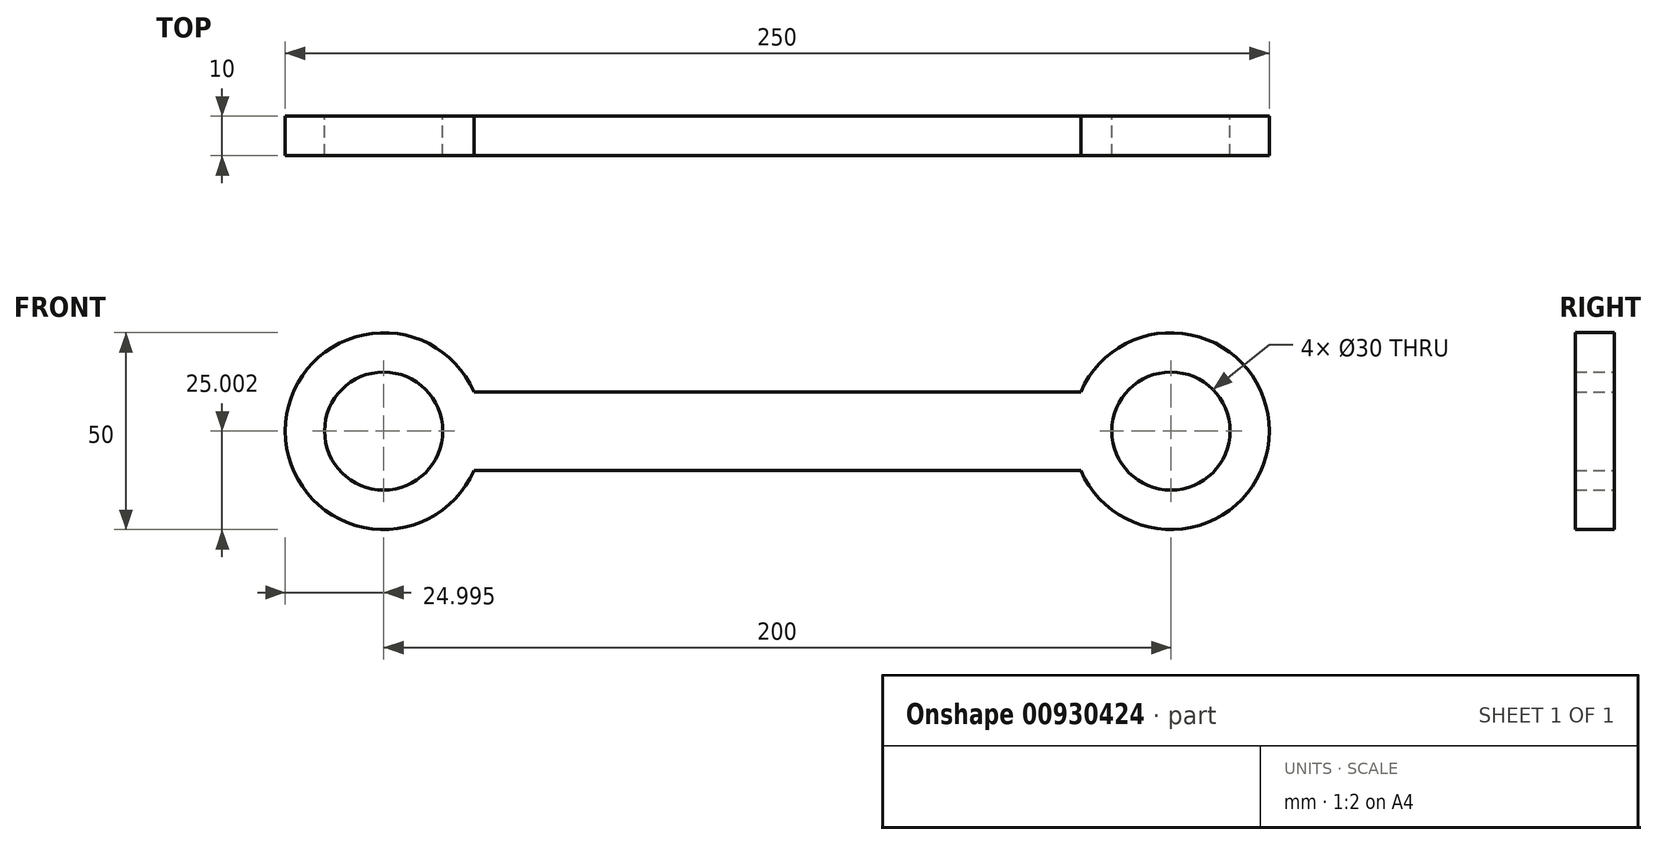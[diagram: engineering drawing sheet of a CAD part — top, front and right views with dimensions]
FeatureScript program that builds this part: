
annotation { "Feature Type Name" : "Feature", "Feature Type Description" : "" }
export const myFeature = defineFeature(function(context is Context, id is Id, definition is map)
    precondition{}
    {
        {
            var Q0;
            Q0=qCreatedBy(makeId("Front.planeOp"),FACE);
            var sketch = newSketch(context, id + "F0", { "sketchPlane" : qUnion([Q0])});
            skLineSegment(sketch, "E0.bottom", {"start": v(235.24, 10.47) * mm, "end": v(35.24, 10.47) * mm});
            skLineSegment(sketch, "E0.top", {"start": v(235.24, 30.47) * mm, "end": v(35.24, 30.47) * mm});
            skLineSegment(sketch, "E0.left", {"start": v(235.24, 10.47) * mm, "end": v(235.24, 30.47) * mm});
            skLineSegment(sketch, "E0.right", {"start": v(35.24, 10.47) * mm, "end": v(35.24, 30.47) * mm});
            skCircle(sketch, "E1", {"center": v(235.24, 20.47) * mm, "radius": 25 * mm});
            skCircle(sketch, "E2", {"center": v(235.24, 20.47) * mm, "radius": 15 * mm});
            skCircle(sketch, "E3", {"center": v(35.24, 20.47) * mm, "radius": 25 * mm});
            skCircle(sketch, "E4", {"center": v(35.24, 20.47) * mm, "radius": 15 * mm});
            skSolve(sketch);
        }
        {
            var Q0;
            {var subQ0=sQuery(id+"F0.wireOp",EDGE,"E1");var subQ1=sQuery(id+"F0.wireOp",EDGE,"E0.bottom");var subQ2=makeQuery(id+"F0.imprint","INTERSECT",VERTEX,{"derivedFrom":[subQ1,subQ0]});Q0=makeQuery(id+"F0.imprint","IMPRINT",FACE,{"disambiguationData":[TD([[makeQuery(id+"F0.imprint","IMPRINT",EDGE,{"disambiguationData":[TD([[subQ2,1.0]])],"derivedFrom":subQ1}),1.0]])]});}
            var Q1;
            {var subQ0=sQuery(id+"F0.wireOp",EDGE,"E1");var subQ1=sQuery(id+"F0.wireOp",EDGE,"E0.bottom");var subQ2=makeQuery(id+"F0.imprint","INTERSECT",VERTEX,{"derivedFrom":[subQ1,subQ0]});Q1=makeQuery(id+"F0.imprint","IMPRINT",FACE,{"disambiguationData":[TD([[makeQuery(id+"F0.imprint","IMPRINT",EDGE,{"disambiguationData":[TD([[subQ2,1.0]])],"derivedFrom":subQ1}),-1.0]])]});}
            var Q2;
            {var subQ0=sQuery(id+"F0.wireOp",EDGE,"E1");var subQ1=sQuery(id+"F0.wireOp",EDGE,"E0.bottom");var subQ2=makeQuery(id+"F0.imprint","INTERSECT",VERTEX,{"derivedFrom":[subQ1,subQ0]});Q2=makeQuery(id+"F0.imprint","IMPRINT",FACE,{"disambiguationData":[TD([[makeQuery(id+"F0.imprint","IMPRINT",EDGE,{"disambiguationData":[TD([[subQ2,-1.0]])],"derivedFrom":subQ1}),-1.0]])]});}
            var Q3;
            {var subQ0=sQuery(id+"F0.wireOp",EDGE,"E3");var subQ1=sQuery(id+"F0.wireOp",EDGE,"E0.bottom");var subQ2=makeQuery(id+"F0.imprint","INTERSECT",VERTEX,{"derivedFrom":[subQ1,subQ0]});Q3=makeQuery(id+"F0.imprint","IMPRINT",FACE,{"disambiguationData":[TD([[makeQuery(id+"F0.imprint","IMPRINT",EDGE,{"disambiguationData":[TD([[subQ2,-1.0]])],"derivedFrom":subQ1}),-1.0]])]});}
            var Q4;
            {var subQ0=sQuery(id+"F0.wireOp",EDGE,"E3");var subQ1=sQuery(id+"F0.wireOp",EDGE,"E0.bottom");var subQ2=makeQuery(id+"F0.imprint","INTERSECT",VERTEX,{"derivedFrom":[subQ1,subQ0]});Q4=makeQuery(id+"F0.imprint","IMPRINT",FACE,{"disambiguationData":[TD([[makeQuery(id+"F0.imprint","IMPRINT",EDGE,{"disambiguationData":[TD([[subQ2,-1.0]])],"derivedFrom":subQ1}),1.0]])]});}
            extrude(context, id + "F1", {"entities" : qUnion([Q0, Q1, Q2, Q3, Q4]), "endBound" : BoundingType.SYMMETRIC, "depth" : 10 * mm, "offsetDistance" : 25 * mm});
        }
        {
            var Q0;
            Q0=makeQuery(id+"F1.opExtrude","SWEPT_BODY",BODY,{"disambiguationData":[OSD([sQuery(id+"F0.wireOp",EDGE,"E0.bottom"),sQuery(id+"F0.wireOp",EDGE,"E0.top"),sQuery(id+"F0.wireOp",EDGE,"E1"),sQuery(id+"F0.wireOp",EDGE,"E2"),sQuery(id+"F0.wireOp",EDGE,"E3"),sQuery(id+"F0.wireOp",EDGE,"E4")])]});
            transform(context, id + "F2", {"entities" : qUnion([Q0]), "transformType" : TransformType.TRANSLATION_3D, "dx" : 0 * mm, "dy" : 0 * mm, "dz" : 0 * mm, "makeCopy" : true});
        }
    });
